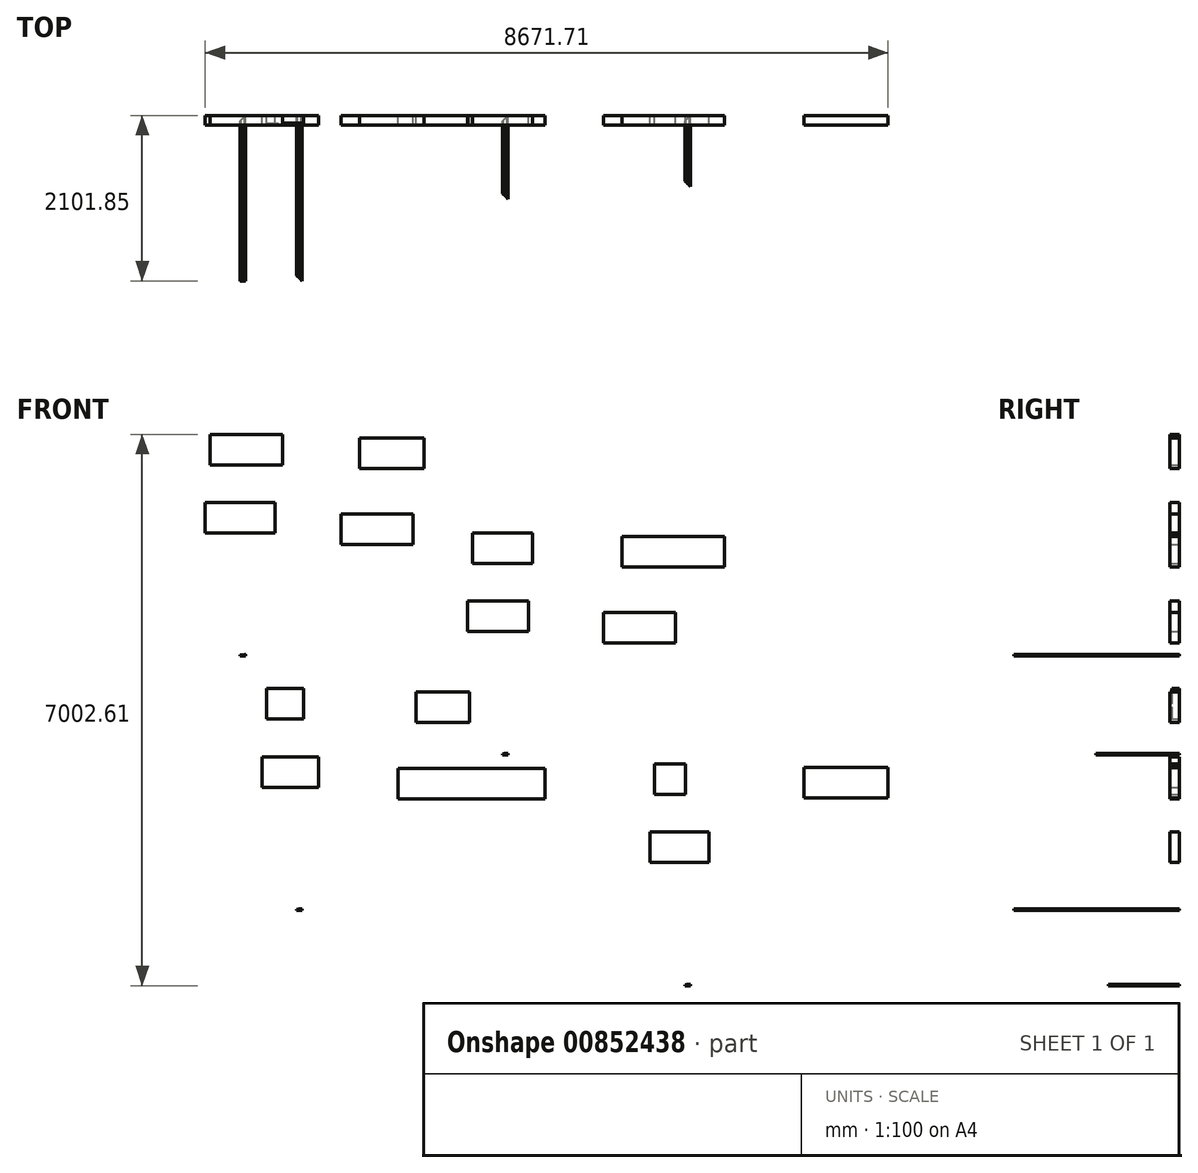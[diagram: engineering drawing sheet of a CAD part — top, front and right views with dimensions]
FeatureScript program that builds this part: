
annotation { "Feature Type Name" : "Feature", "Feature Type Description" : "" }
export const myFeature = defineFeature(function(context is Context, id is Id, definition is map)
    precondition{}
    {
        {
            var Q0;
            Q0=qCreatedBy(makeId("Front.planeOp"),FACE);
            var sketch = newSketch(context, id + "F0", { "sketchPlane" : qUnion([Q0])});
            skLineSegment(sketch, "E0.bottom", {"start": v(-416.95, 244.7) * mm, "end": v(503.8, 244.7) * mm});
            skLineSegment(sketch, "E0.top", {"start": v(-416.95, -142.64) * mm, "end": v(503.8, -142.64) * mm});
            skLineSegment(sketch, "E0.left", {"start": v(-416.95, 244.7) * mm, "end": v(-416.95, -142.64) * mm});
            skLineSegment(sketch, "E0.right", {"start": v(503.8, 244.7) * mm, "end": v(503.8, -142.64) * mm});
            skLineSegment(sketch, "E1.bottom", {"start": v(-477.88, -620.2) * mm, "end": v(411.12, -620.2) * mm});
            skLineSegment(sketch, "E1.top", {"start": v(-477.88, -1007.55) * mm, "end": v(411.12, -1007.55) * mm});
            skLineSegment(sketch, "E1.left", {"start": v(-477.88, -620.2) * mm, "end": v(-477.88, -1007.55) * mm});
            skLineSegment(sketch, "E1.right", {"start": v(411.12, -620.2) * mm, "end": v(411.12, -1007.55) * mm});
            skLineSegment(sketch, "E2.bottom", {"start": v(1478.97, 200.6) * mm, "end": v(2298.12, 200.6) * mm});
            skLineSegment(sketch, "E2.top", {"start": v(1478.97, -186.75) * mm, "end": v(2298.12, -186.75) * mm});
            skLineSegment(sketch, "E2.left", {"start": v(1478.97, 200.6) * mm, "end": v(1478.97, -186.75) * mm});
            skLineSegment(sketch, "E2.right", {"start": v(2298.12, 200.6) * mm, "end": v(2298.12, -186.75) * mm});
            skLineSegment(sketch, "E3.bottom", {"start": v(1249.59, -767.08) * mm, "end": v(2163.99, -767.08) * mm});
            skLineSegment(sketch, "E3.top", {"start": v(1249.59, -1154.43) * mm, "end": v(2163.99, -1154.43) * mm});
            skLineSegment(sketch, "E3.left", {"start": v(1249.59, -767.08) * mm, "end": v(1249.59, -1154.43) * mm});
            skLineSegment(sketch, "E3.right", {"start": v(2163.99, -767.08) * mm, "end": v(2163.99, -1154.43) * mm});
            skLineSegment(sketch, "E4.bottom", {"start": v(34.92, -2552.16) * mm, "end": v(22.22, -2552.16) * mm});
            skLineSegment(sketch, "E4.top", {"start": v(34.92, -2571.21) * mm, "end": v(-34.93, -2571.21) * mm});
            skLineSegment(sketch, "E4.left", {"start": v(34.92, -2552.16) * mm, "end": v(34.92, -2571.21) * mm});
            skLineSegment(sketch, "E4.right", {"start": v(-34.93, -2558.51) * mm, "end": v(-34.93, -2571.21) * mm});
            skPoint(sketch, "E5", {"position": v(-34.93, -2558.51) * mm});
            skLineSegment(sketch, "E6", {"start": v(-34.93, -2558.51) * mm, "end": v(34.92, -2558.51) * mm, "construction": true});
            skPoint(sketch, "E7", {"position": v(-22.23, -2558.51) * mm});
            skPoint(sketch, "E8", {"position": v(22.22, -2552.16) * mm});
            skPoint(sketch, "E9", {"position": v(-22.23, -2561.69) * mm});
            skPoint(sketch, "E10", {"position": v(22.22, -2555.34) * mm});
            skLineSegment(sketch, "E11", {"start": v(-34.93, -2558.51) * mm, "end": v(-22.23, -2558.51) * mm});
            skLineSegment(sketch, "E12", {"start": v(-22.23, -2561.69) * mm, "end": v(-22.23, -2558.51) * mm});
            skLineSegment(sketch, "E13", {"start": v(22.22, -2555.34) * mm, "end": v(22.22, -2552.16) * mm});
            skFitSpline(sketch, "E14", {"points": [v(22.22, -2555.34) * mm, v(0, -2555.34) * mm, v(-22.23, -2561.69) * mm], "startDerivative": vector(-49.35, 19.24) * mm, "endDerivative": vector(-37.36, -33.66) * mm});
            skLineSegment(sketch, "E15.bottom", {"start": v(2916.7, -1008.06) * mm, "end": v(3678.7, -1008.06) * mm});
            skLineSegment(sketch, "E15.top", {"start": v(2916.7, -1395.4) * mm, "end": v(3678.7, -1395.4) * mm});
            skLineSegment(sketch, "E15.left", {"start": v(2916.7, -1008.06) * mm, "end": v(2916.7, -1395.4) * mm});
            skLineSegment(sketch, "E15.right", {"start": v(3678.7, -1008.06) * mm, "end": v(3678.7, -1395.4) * mm});
            skLineSegment(sketch, "E16.bottom", {"start": v(2855.77, -1872.97) * mm, "end": v(3630.47, -1872.97) * mm});
            skLineSegment(sketch, "E16.top", {"start": v(2855.77, -2260.32) * mm, "end": v(3630.47, -2260.32) * mm});
            skLineSegment(sketch, "E16.left", {"start": v(2855.77, -1872.97) * mm, "end": v(2855.77, -2260.32) * mm});
            skLineSegment(sketch, "E16.right", {"start": v(3630.47, -1872.97) * mm, "end": v(3630.47, -2260.32) * mm});
            skLineSegment(sketch, "E17.bottom", {"start": v(4812.62, -1052.16) * mm, "end": v(6114.37, -1052.16) * mm});
            skLineSegment(sketch, "E17.top", {"start": v(4812.62, -1439.51) * mm, "end": v(6114.37, -1439.51) * mm});
            skLineSegment(sketch, "E17.left", {"start": v(4812.62, -1052.16) * mm, "end": v(4812.62, -1439.51) * mm});
            skLineSegment(sketch, "E17.right", {"start": v(6114.37, -1052.16) * mm, "end": v(6114.37, -1439.51) * mm});
            skLineSegment(sketch, "E18.bottom", {"start": v(4583.24, -2019.85) * mm, "end": v(5494.47, -2019.85) * mm});
            skLineSegment(sketch, "E18.top", {"start": v(4583.24, -2407.2) * mm, "end": v(5494.47, -2407.2) * mm});
            skLineSegment(sketch, "E18.left", {"start": v(4583.24, -2019.85) * mm, "end": v(4583.24, -2407.2) * mm});
            skLineSegment(sketch, "E18.right", {"start": v(5494.47, -2019.85) * mm, "end": v(5494.47, -2407.2) * mm});
            skLineSegment(sketch, "E19.bottom", {"start": v(3368.58, -3804.93) * mm, "end": v(3355.88, -3804.93) * mm});
            skLineSegment(sketch, "E19.top", {"start": v(3368.58, -3823.98) * mm, "end": v(3298.73, -3823.98) * mm});
            skLineSegment(sketch, "E19.left", {"start": v(3368.58, -3804.93) * mm, "end": v(3368.58, -3823.98) * mm});
            skLineSegment(sketch, "E19.right", {"start": v(3298.73, -3811.28) * mm, "end": v(3298.73, -3823.98) * mm});
            skPoint(sketch, "E20", {"position": v(3298.73, -3811.28) * mm});
            skLineSegment(sketch, "E21", {"start": v(3298.73, -3811.28) * mm, "end": v(3368.58, -3811.28) * mm, "construction": true});
            skPoint(sketch, "E22", {"position": v(3311.43, -3811.28) * mm});
            skPoint(sketch, "E23", {"position": v(3355.88, -3804.93) * mm});
            skPoint(sketch, "E24", {"position": v(3311.43, -3814.46) * mm});
            skPoint(sketch, "E25", {"position": v(3355.88, -3808.1) * mm});
            skLineSegment(sketch, "E26", {"start": v(3298.73, -3811.28) * mm, "end": v(3311.43, -3811.28) * mm});
            skLineSegment(sketch, "E27", {"start": v(3311.43, -3814.46) * mm, "end": v(3311.43, -3811.28) * mm});
            skLineSegment(sketch, "E28", {"start": v(3355.88, -3808.1) * mm, "end": v(3355.88, -3804.93) * mm});
            skFitSpline(sketch, "E29", {"points": [v(3355.88, -3808.1) * mm, v(3333.65, -3808.1) * mm, v(3311.43, -3814.46) * mm], "startDerivative": vector(-49.35, 19.24) * mm, "endDerivative": vector(-37.36, -33.66) * mm});
            skLineSegment(sketch, "E30.bottom", {"start": v(301.38, -2984.14) * mm, "end": v(771.28, -2984.14) * mm});
            skLineSegment(sketch, "E30.top", {"start": v(301.38, -3371.5) * mm, "end": v(771.28, -3371.5) * mm});
            skLineSegment(sketch, "E30.left", {"start": v(301.38, -2984.14) * mm, "end": v(301.38, -3371.5) * mm});
            skLineSegment(sketch, "E30.right", {"start": v(771.28, -2984.14) * mm, "end": v(771.28, -3371.5) * mm});
            skLineSegment(sketch, "E31.bottom", {"start": v(240.45, -3849.06) * mm, "end": v(964.35, -3849.06) * mm});
            skLineSegment(sketch, "E31.top", {"start": v(240.45, -4236.4) * mm, "end": v(964.35, -4236.4) * mm});
            skLineSegment(sketch, "E31.left", {"start": v(240.45, -3849.06) * mm, "end": v(240.45, -4236.4) * mm});
            skLineSegment(sketch, "E31.right", {"start": v(964.35, -3849.06) * mm, "end": v(964.35, -4236.4) * mm});
            skLineSegment(sketch, "E32.bottom", {"start": v(2197.3, -3028.25) * mm, "end": v(2876.75, -3028.25) * mm});
            skLineSegment(sketch, "E32.top", {"start": v(2197.3, -3415.6) * mm, "end": v(2876.75, -3415.6) * mm});
            skLineSegment(sketch, "E32.left", {"start": v(2197.3, -3028.25) * mm, "end": v(2197.3, -3415.6) * mm});
            skLineSegment(sketch, "E32.right", {"start": v(2876.75, -3028.25) * mm, "end": v(2876.75, -3415.6) * mm});
            skLineSegment(sketch, "E33.bottom", {"start": v(1967.92, -3995.94) * mm, "end": v(3835.78, -3995.94) * mm});
            skLineSegment(sketch, "E33.top", {"start": v(1967.92, -4383.29) * mm, "end": v(3835.78, -4383.29) * mm});
            skLineSegment(sketch, "E33.left", {"start": v(1967.92, -3995.94) * mm, "end": v(1967.92, -4383.29) * mm});
            skLineSegment(sketch, "E33.right", {"start": v(3835.78, -3995.94) * mm, "end": v(3835.78, -4383.29) * mm});
            skLineSegment(sketch, "E34.bottom", {"start": v(753.25, -5781.02) * mm, "end": v(740.55, -5781.02) * mm});
            skLineSegment(sketch, "E34.top", {"start": v(753.25, -5800.07) * mm, "end": v(683.4, -5800.07) * mm});
            skLineSegment(sketch, "E34.left", {"start": v(753.25, -5781.02) * mm, "end": v(753.25, -5800.07) * mm});
            skLineSegment(sketch, "E34.right", {"start": v(683.4, -5787.37) * mm, "end": v(683.4, -5800.07) * mm});
            skPoint(sketch, "E35", {"position": v(683.4, -5787.37) * mm});
            skLineSegment(sketch, "E36", {"start": v(683.4, -5787.37) * mm, "end": v(753.25, -5787.37) * mm, "construction": true});
            skPoint(sketch, "E37", {"position": v(696.1, -5787.37) * mm});
            skPoint(sketch, "E38", {"position": v(740.55, -5781.02) * mm});
            skPoint(sketch, "E39", {"position": v(696.1, -5790.54) * mm});
            skPoint(sketch, "E40", {"position": v(740.55, -5784.2) * mm});
            skLineSegment(sketch, "E41", {"start": v(683.4, -5787.37) * mm, "end": v(696.1, -5787.37) * mm});
            skLineSegment(sketch, "E42", {"start": v(696.1, -5790.54) * mm, "end": v(696.1, -5787.37) * mm});
            skLineSegment(sketch, "E43", {"start": v(740.55, -5784.2) * mm, "end": v(740.55, -5781.02) * mm});
            skFitSpline(sketch, "E44", {"points": [v(740.55, -5784.2) * mm, v(718.33, -5784.2) * mm, v(696.1, -5790.54) * mm], "startDerivative": vector(-49.35, 19.24) * mm, "endDerivative": vector(-37.36, -33.66) * mm});
            skLineSegment(sketch, "E45.bottom", {"start": v(5231.1, -3941.97) * mm, "end": v(5624.8, -3941.97) * mm});
            skLineSegment(sketch, "E45.top", {"start": v(5231.1, -4329.32) * mm, "end": v(5624.8, -4329.32) * mm});
            skLineSegment(sketch, "E45.left", {"start": v(5231.1, -3941.97) * mm, "end": v(5231.1, -4329.32) * mm});
            skLineSegment(sketch, "E45.right", {"start": v(5624.8, -3941.97) * mm, "end": v(5624.8, -4329.32) * mm});
            skLineSegment(sketch, "E46.bottom", {"start": v(5170.18, -4806.89) * mm, "end": v(5919.48, -4806.89) * mm});
            skLineSegment(sketch, "E46.top", {"start": v(5170.18, -5194.24) * mm, "end": v(5919.48, -5194.24) * mm});
            skLineSegment(sketch, "E46.left", {"start": v(5170.18, -4806.89) * mm, "end": v(5170.18, -5194.24) * mm});
            skLineSegment(sketch, "E46.right", {"start": v(5919.48, -4806.89) * mm, "end": v(5919.48, -5194.24) * mm});
            skLineSegment(sketch, "E47.bottom", {"start": v(7127.03, -3986.08) * mm, "end": v(8193.83, -3986.08) * mm});
            skLineSegment(sketch, "E47.top", {"start": v(7127.03, -4373.43) * mm, "end": v(8193.83, -4373.43) * mm});
            skLineSegment(sketch, "E47.left", {"start": v(7127.03, -3986.08) * mm, "end": v(7127.03, -4373.43) * mm});
            skLineSegment(sketch, "E47.right", {"start": v(8193.83, -3986.08) * mm, "end": v(8193.83, -4373.43) * mm});
            skLineSegment(sketch, "E48.bottom", {"start": v(6897.65, -4953.77) * mm, "end": v(7812.05, -4953.77) * mm});
            skLineSegment(sketch, "E48.top", {"start": v(6897.65, -5341.12) * mm, "end": v(7812.05, -5341.12) * mm});
            skLineSegment(sketch, "E48.left", {"start": v(6897.65, -4953.77) * mm, "end": v(6897.65, -5341.12) * mm});
            skLineSegment(sketch, "E48.right", {"start": v(7812.05, -4953.77) * mm, "end": v(7812.05, -5341.12) * mm});
            skLineSegment(sketch, "E49.bottom", {"start": v(5682.98, -6738.85) * mm, "end": v(5670.28, -6738.85) * mm});
            skLineSegment(sketch, "E49.top", {"start": v(5682.98, -6757.9) * mm, "end": v(5613.13, -6757.9) * mm});
            skLineSegment(sketch, "E49.left", {"start": v(5682.98, -6738.85) * mm, "end": v(5682.98, -6757.9) * mm});
            skLineSegment(sketch, "E49.right", {"start": v(5613.13, -6745.2) * mm, "end": v(5613.13, -6757.9) * mm});
            skPoint(sketch, "E50", {"position": v(5613.13, -6745.2) * mm});
            skLineSegment(sketch, "E51", {"start": v(5613.13, -6745.2) * mm, "end": v(5682.98, -6745.2) * mm, "construction": true});
            skPoint(sketch, "E52", {"position": v(5625.83, -6745.2) * mm});
            skPoint(sketch, "E53", {"position": v(5670.28, -6738.85) * mm});
            skPoint(sketch, "E54", {"position": v(5625.83, -6748.37) * mm});
            skPoint(sketch, "E55", {"position": v(5670.28, -6742.02) * mm});
            skLineSegment(sketch, "E56", {"start": v(5613.13, -6745.2) * mm, "end": v(5625.83, -6745.2) * mm});
            skLineSegment(sketch, "E57", {"start": v(5625.83, -6748.37) * mm, "end": v(5625.83, -6745.2) * mm});
            skLineSegment(sketch, "E58", {"start": v(5670.28, -6742.02) * mm, "end": v(5670.28, -6738.85) * mm});
            skFitSpline(sketch, "E59", {"points": [v(5670.28, -6742.02) * mm, v(5648.06, -6742.02) * mm, v(5625.83, -6748.37) * mm], "startDerivative": vector(-49.35, 19.24) * mm, "endDerivative": vector(-37.36, -33.66) * mm});
            skSolve(sketch);
        }
        {
            var Q0;
            Q0=makeQuery(id+"F0.imprint","IMPRINT",FACE,{"disambiguationData":[TD([[makeQuery(id+"F0.imprint","IMPRINT",EDGE,{"derivedFrom":sQuery(id+"F0.wireOp",EDGE,"E0.bottom")}),-1.0]])]});
            var Q1;
            Q1=makeQuery(id+"F0.imprint","IMPRINT",FACE,{"disambiguationData":[TD([[makeQuery(id+"F0.imprint","IMPRINT",EDGE,{"derivedFrom":sQuery(id+"F0.wireOp",EDGE,"E1.bottom")}),-1.0]])]});
            var Q2;
            Q2=makeQuery(id+"F0.imprint","IMPRINT",FACE,{"disambiguationData":[TD([[makeQuery(id+"F0.imprint","IMPRINT",EDGE,{"derivedFrom":sQuery(id+"F0.wireOp",EDGE,"E2.bottom")}),-1.0]])]});
            var Q3;
            Q3=makeQuery(id+"F0.imprint","IMPRINT",FACE,{"disambiguationData":[TD([[makeQuery(id+"F0.imprint","IMPRINT",EDGE,{"derivedFrom":sQuery(id+"F0.wireOp",EDGE,"E3.bottom")}),-1.0]])]});
            extrude(context, id + "F1", {"entities" : qUnion([Q0, Q1, Q2, Q3]), "depth" : 123.82 * mm, "offsetDistance" : 25.4 * mm});
        }
        {
            var Q0;
            Q0=makeQuery(id+"F0.imprint","IMPRINT",FACE,{"disambiguationData":[TD([[makeQuery(id+"F0.imprint","IMPRINT",EDGE,{"derivedFrom":sQuery(id+"F0.wireOp",EDGE,"E4.bottom")}),1.0]])]});
            extrude(context, id + "F2", {"entities" : qUnion([Q0]), "depth" : 2101.85 * mm, "offsetDistance" : 25.4 * mm});
        }
        {
            var Q0;
            Q0=makeQuery(id+"F2.opExtrude","SWEPT_EDGE",EDGE,{"disambiguationData":[OSD([sQuery(id+"F0.wireOp",EDGE,"E4.right"),sQuery(id+"F0.wireOp",EDGE,"E11")])]});
            var Q1;
            Q1=makeQuery(id+"F2.opExtrude","SWEPT_EDGE",EDGE,{"disambiguationData":[OSD([sQuery(id+"F0.wireOp",EDGE,"E11"),sQuery(id+"F0.wireOp",EDGE,"E12")])]});
            var Q2;
            Q2=makeQuery(id+"F2.opExtrude","SWEPT_EDGE",EDGE,{"disambiguationData":[OSD([sQuery(id+"F0.wireOp",EDGE,"E4.bottom"),sQuery(id+"F0.wireOp",EDGE,"E13")])]});
            var Q3;
            Q3=makeQuery(id+"F2.opExtrude","SWEPT_EDGE",EDGE,{"disambiguationData":[OSD([sQuery(id+"F0.wireOp",EDGE,"E4.bottom"),sQuery(id+"F0.wireOp",EDGE,"E4.left")])]});
            fillet(context, id + "F3", {"entities" : qUnion([Q0, Q1, Q2, Q3]), "radius" : 3.17 * mm, "tangentPropagation" : true, "allowEdgeOverflow" : false});
        }
        {
            var Q0;
            Q0=makeQuery(id+"F2.opExtrude","CAP_EDGE",EDGE,{"disambiguationData":[OSD([sQuery(id+"F0.wireOp",EDGE,"E4.right")])],"isStart":true});
            chamfer(context, id + "F4", {"entities" : qUnion([Q0]), "width" : 69.85 * mm, "tangentPropagation" : true});
        }
        {
            var Q0;
            Q0=makeQuery(id+"F0.imprint","IMPRINT",FACE,{"disambiguationData":[TD([[makeQuery(id+"F0.imprint","IMPRINT",EDGE,{"derivedFrom":sQuery(id+"F0.wireOp",EDGE,"E34.bottom")}),1.0]])]});
            extrude(context, id + "F5", {"entities" : qUnion([Q0]), "depth" : 2101.85 * mm, "offsetDistance" : 25.4 * mm});
        }
        {
            var Q0;
            Q0=makeQuery(id+"F5.opExtrude","CAP_EDGE",EDGE,{"disambiguationData":[OSD([sQuery(id+"F0.wireOp",EDGE,"E34.right")])],"isStart":false});
            chamfer(context, id + "F6", {"entities" : qUnion([Q0]), "width" : 69.85 * mm, "tangentPropagation" : true});
        }
        {
            var Q0;
            Q0=makeQuery(id+"F0.imprint","IMPRINT",FACE,{"disambiguationData":[TD([[makeQuery(id+"F0.imprint","IMPRINT",EDGE,{"derivedFrom":sQuery(id+"F0.wireOp",EDGE,"E15.bottom")}),-1.0]])]});
            var Q1;
            Q1=makeQuery(id+"F0.imprint","IMPRINT",FACE,{"disambiguationData":[TD([[makeQuery(id+"F0.imprint","IMPRINT",EDGE,{"derivedFrom":sQuery(id+"F0.wireOp",EDGE,"E17.bottom")}),-1.0]])]});
            extrude(context, id + "F7", {"entities" : qUnion([Q0, Q1]), "depth" : 123.82 * mm, "offsetDistance" : 25.4 * mm});
        }
        {
            var Q0;
            Q0=makeQuery(id+"F0.imprint","IMPRINT",FACE,{"disambiguationData":[TD([[makeQuery(id+"F0.imprint","IMPRINT",EDGE,{"derivedFrom":sQuery(id+"F0.wireOp",EDGE,"E16.bottom")}),-1.0]])]});
            extrude(context, id + "F8", {"entities" : qUnion([Q0]), "depth" : 123.82 * mm, "offsetDistance" : 25.4 * mm});
        }
        {
            var Q0;
            Q0=makeQuery(id+"F0.imprint","IMPRINT",FACE,{"disambiguationData":[TD([[makeQuery(id+"F0.imprint","IMPRINT",EDGE,{"derivedFrom":sQuery(id+"F0.wireOp",EDGE,"E18.bottom")}),-1.0]])]});
            extrude(context, id + "F9", {"entities" : qUnion([Q0]), "depth" : 123.82 * mm, "offsetDistance" : 25.4 * mm});
        }
        {
            var Q0;
            Q0=makeQuery(id+"F0.imprint","IMPRINT",FACE,{"disambiguationData":[TD([[makeQuery(id+"F0.imprint","IMPRINT",EDGE,{"derivedFrom":sQuery(id+"F0.wireOp",EDGE,"E32.bottom")}),-1.0]])]});
            extrude(context, id + "F10", {"entities" : qUnion([Q0]), "depth" : 123.82 * mm, "offsetDistance" : 25.4 * mm});
        }
        {
            var Q0;
            Q0=makeQuery(id+"F0.imprint","IMPRINT",FACE,{"disambiguationData":[TD([[makeQuery(id+"F0.imprint","IMPRINT",EDGE,{"derivedFrom":sQuery(id+"F0.wireOp",EDGE,"E30.bottom")}),-1.0]])]});
            extrude(context, id + "F11", {"entities" : qUnion([Q0]), "depth" : 95.25 * mm, "offsetDistance" : 25.4 * mm});
        }
        {
            var Q0;
            Q0=makeQuery(id+"F0.imprint","IMPRINT",FACE,{"disambiguationData":[TD([[makeQuery(id+"F0.imprint","IMPRINT",EDGE,{"derivedFrom":sQuery(id+"F0.wireOp",EDGE,"E31.bottom")}),-1.0]])]});
            extrude(context, id + "F12", {"entities" : qUnion([Q0]), "depth" : 123.82 * mm, "offsetDistance" : 25.4 * mm});
        }
        {
            var Q0;
            Q0=makeQuery(id+"F0.imprint","IMPRINT",FACE,{"disambiguationData":[TD([[makeQuery(id+"F0.imprint","IMPRINT",EDGE,{"derivedFrom":sQuery(id+"F0.wireOp",EDGE,"E33.bottom")}),-1.0]])]});
            extrude(context, id + "F13", {"entities" : qUnion([Q0]), "depth" : 123.82 * mm, "offsetDistance" : 25.4 * mm});
        }
        {
            var Q0;
            Q0=makeQuery(id+"F0.imprint","IMPRINT",FACE,{"disambiguationData":[TD([[makeQuery(id+"F0.imprint","IMPRINT",EDGE,{"derivedFrom":sQuery(id+"F0.wireOp",EDGE,"E45.bottom")}),-1.0]])]});
            extrude(context, id + "F14", {"entities" : qUnion([Q0]), "depth" : 123.82 * mm, "offsetDistance" : 25.4 * mm});
        }
        {
            var Q0;
            Q0=makeQuery(id+"F0.imprint","IMPRINT",FACE,{"disambiguationData":[TD([[makeQuery(id+"F0.imprint","IMPRINT",EDGE,{"derivedFrom":sQuery(id+"F0.wireOp",EDGE,"E47.bottom")}),-1.0]])]});
            extrude(context, id + "F15", {"entities" : qUnion([Q0]), "depth" : 123.82 * mm, "offsetDistance" : 25.4 * mm});
        }
        {
            var Q0;
            Q0=makeQuery(id+"F0.imprint","IMPRINT",FACE,{"disambiguationData":[TD([[makeQuery(id+"F0.imprint","IMPRINT",EDGE,{"derivedFrom":sQuery(id+"F0.wireOp",EDGE,"E49.bottom")}),1.0]])]});
            extrude(context, id + "F16", {"entities" : qUnion([Q0]), "depth" : 901.7 * mm, "offsetDistance" : 25.4 * mm});
        }
        {
            var Q0;
            Q0=makeQuery(id+"F16.opExtrude","CAP_EDGE",EDGE,{"disambiguationData":[OSD([sQuery(id+"F0.wireOp",EDGE,"E49.right")])],"isStart":false});
            var Q1;
            Q1=makeQuery(id+"F16.opExtrude","CAP_EDGE",EDGE,{"disambiguationData":[OSD([sQuery(id+"F0.wireOp",EDGE,"E49.right")])],"isStart":true});
            chamfer(context, id + "F17", {"entities" : qUnion([Q0, Q1]), "width" : 69.85 * mm, "tangentPropagation" : true});
        }
        {
            var Q0;
            Q0=makeQuery(id+"F0.imprint","IMPRINT",FACE,{"disambiguationData":[TD([[makeQuery(id+"F0.imprint","IMPRINT",EDGE,{"derivedFrom":sQuery(id+"F0.wireOp",EDGE,"E19.bottom")}),1.0]])]});
            extrude(context, id + "F18", {"entities" : qUnion([Q0]), "depth" : 1060.45 * mm, "offsetDistance" : 25.4 * mm});
        }
        {
            var Q0;
            Q0=makeQuery(id+"F18.opExtrude","CAP_EDGE",EDGE,{"disambiguationData":[OSD([sQuery(id+"F0.wireOp",EDGE,"E19.right")])],"isStart":false});
            var Q1;
            Q1=makeQuery(id+"F18.opExtrude","CAP_EDGE",EDGE,{"disambiguationData":[OSD([sQuery(id+"F0.wireOp",EDGE,"E19.right")])],"isStart":true});
            chamfer(context, id + "F19", {"entities" : qUnion([Q0, Q1]), "width" : 69.85 * mm, "tangentPropagation" : true});
        }
        {
            var Q0;
            Q0=makeQuery(id+"F0.imprint","IMPRINT",FACE,{"disambiguationData":[TD([[makeQuery(id+"F0.imprint","IMPRINT",EDGE,{"derivedFrom":sQuery(id+"F0.wireOp",EDGE,"E46.bottom")}),-1.0]])]});
            extrude(context, id + "F20", {"entities" : qUnion([Q0]), "depth" : 123.82 * mm, "offsetDistance" : 25.4 * mm});
        }
    });
